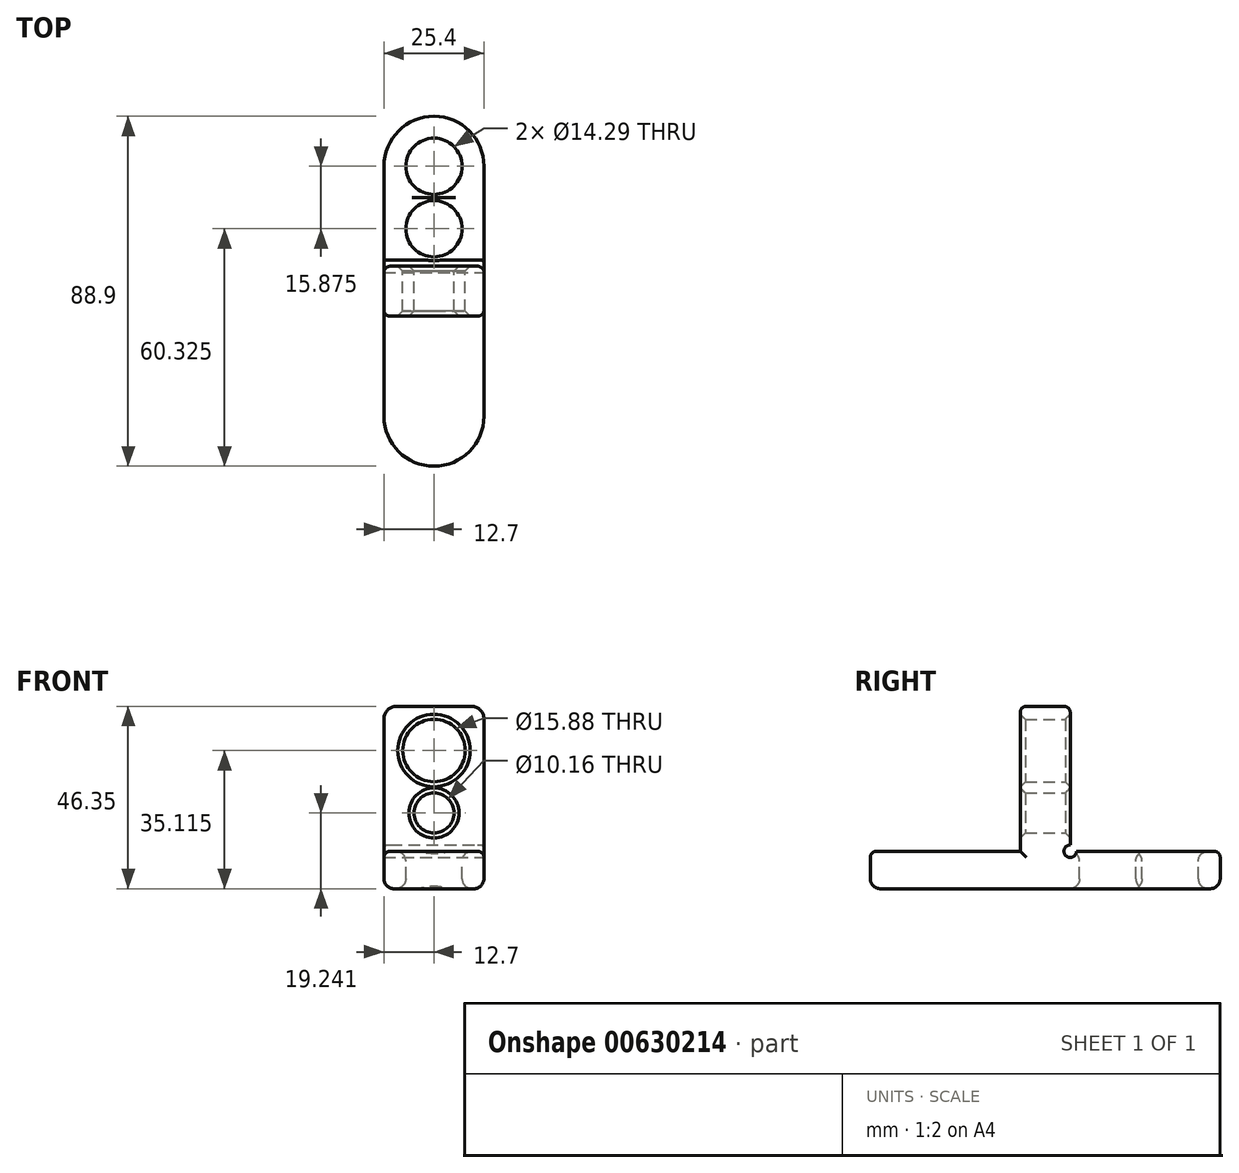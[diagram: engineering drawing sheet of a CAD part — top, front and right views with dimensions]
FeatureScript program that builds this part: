
annotation { "Feature Type Name" : "Feature", "Feature Type Description" : "" }
export const myFeature = defineFeature(function(context is Context, id is Id, definition is map)
    precondition{}
    {
        {
            var Q0;
            Q0=qCreatedBy(makeId("Top.planeOp"),FACE);
            var sketch = newSketch(context, id + "F0", { "sketchPlane" : qUnion([Q0])});
            skLineSegment(sketch, "E0.bottom", {"start": v(-12.7, 44.45) * mm, "end": v(12.7, 44.45) * mm});
            skLineSegment(sketch, "E0.top", {"start": v(-12.7, -44.45) * mm, "end": v(12.7, -44.45) * mm});
            skLineSegment(sketch, "E0.left", {"start": v(-12.7, 44.45) * mm, "end": v(-12.7, -44.45) * mm});
            skLineSegment(sketch, "E0.right", {"start": v(12.7, 44.45) * mm, "end": v(12.7, -44.45) * mm});
            skPoint(sketch, "E0.middle", {"position": v(0, 0) * mm});
            skSolve(sketch);
        }
        {
            var Q0;
            Q0=makeQuery(id+"F0.imprint","IMPRINT",FACE,{"disambiguationData":[TD([[makeQuery(id+"F0.imprint","IMPRINT",EDGE,{"derivedFrom":sQuery(id+"F0.wireOp",EDGE,"E0.bottom")}),-1.0]])]});
            extrude(context, id + "F1", {"entities" : qUnion([Q0]), "depth" : 9.52 * mm, "offsetDistance" : 25.4 * mm});
        }
        {
            var Q0;
            Q0=makeQuery(id+"F1.opExtrude","CAP_FACE",FACE,{"disambiguationData":[OSD([sQuery(id+"F0.wireOp",EDGE,"E0.bottom"),sQuery(id+"F0.wireOp",EDGE,"E0.top"),sQuery(id+"F0.wireOp",EDGE,"E0.left"),sQuery(id+"F0.wireOp",EDGE,"E0.right")])],"isStart":false});
            var sketch = newSketch(context, id + "F2", { "sketchPlane" : qUnion([Q0])});
            skLineSegment(sketch, "E1.bottom", {"start": v(-12.7, -6.35) * mm, "end": v(12.7, -6.35) * mm});
            skLineSegment(sketch, "E1.top", {"start": v(-12.7, 6.35) * mm, "end": v(12.7, 6.35) * mm});
            skLineSegment(sketch, "E1.left", {"start": v(-12.7, -6.35) * mm, "end": v(-12.7, 6.35) * mm});
            skLineSegment(sketch, "E1.right", {"start": v(12.7, -6.35) * mm, "end": v(12.7, 6.35) * mm});
            skPoint(sketch, "E1.middle", {"position": v(0, 0) * mm});
            skSolve(sketch);
        }
        {
            var Q0;
            Q0=makeQuery(id+"F2.imprint","IMPRINT",FACE,{"disambiguationData":[TD([[makeQuery(id+"F2.imprint","IMPRINT",EDGE,{"derivedFrom":sQuery(id+"F2.wireOp",EDGE,"E1.bottom")}),1.0]])]});
            extrude(context, id + "F3", {"entities" : qUnion([Q0]), "operationType" : NewBodyOperationType.ADD, "depth" : 36.83 * mm, "offsetDistance" : 25.4 * mm});
        }
        {
            var Q0;
            Q0=makeQuery(id+"F3.opExtrude","SWEPT_FACE",FACE,{"disambiguationData":[OSD([sQuery(id+"F2.wireOp",EDGE,"E1.top")])]});
            var sketch = newSketch(context, id + "F4", { "sketchPlane" : qUnion([Q0])});
            skCircle(sketch, "E2", {"center": v(0, 19.24) * mm, "radius": 5.08 * mm});
            skPoint(sketch, "E2.centerSnap0", {"position": v(0, 46.35) * mm});
            skCircle(sketch, "E3", {"center": v(0, 35.12) * mm, "radius": 7.94 * mm});
            skSolve(sketch);
        }
        {
            var Q0;
            Q0=makeQuery(id+"F4.imprint","IMPRINT",FACE,{"disambiguationData":[TD([[makeQuery(id+"F4.imprint","IMPRINT",EDGE,{"derivedFrom":sQuery(id+"F4.wireOp",EDGE,"E2")}),1.0]])]});
            var Q1;
            Q1=makeQuery(id+"F4.imprint","IMPRINT",FACE,{"disambiguationData":[TD([[makeQuery(id+"F4.imprint","IMPRINT",EDGE,{"derivedFrom":sQuery(id+"F4.wireOp",EDGE,"E3")}),1.0]])]});
            extrude(context, id + "F5", {"entities" : qUnion([Q0, Q1]), "operationType" : NewBodyOperationType.REMOVE, "endBound" : BoundingType.THROUGH_ALL, "oppositeDirection" : true, "depth" : 25.4 * mm, "offsetDistance" : 25.4 * mm});
        }
        {
            var Q0;
            Q0=makeQuery(id+"F5.boolean.opBoolean","COPY",FACE,{"derivedFrom":makeQuery(id+"F5.opExtrude","SWEPT_FACE",FACE,{"disambiguationData":[OSD([sQuery(id+"F4.wireOp",EDGE,"E2")])]})});
            var Q1;
            Q1=makeQuery(id+"F5.boolean.opBoolean","COPY",FACE,{"derivedFrom":makeQuery(id+"F5.opExtrude","SWEPT_FACE",FACE,{"disambiguationData":[OSD([sQuery(id+"F4.wireOp",EDGE,"E3")])]})});
            chamfer(context, id + "F6", {"entities" : qUnion([Q0, Q1]), "width" : 1.27 * mm, "tangentPropagation" : true});
        }
        {
            var Q0;
            Q0=makeQuery(id+"F3.opExtrude","CAP_EDGE",EDGE,{"disambiguationData":[OSD([sQuery(id+"F2.wireOp",EDGE,"E1.left")])],"isStart":false});
            var Q1;
            Q1=makeQuery(id+"F3.opExtrude","CAP_EDGE",EDGE,{"disambiguationData":[OSD([sQuery(id+"F2.wireOp",EDGE,"E1.right")])],"isStart":false});
            fillet(context, id + "F7", {"entities" : qUnion([Q0, Q1]), "radius" : 3.17 * mm, "tangentPropagation" : true, "allowEdgeOverflow" : false});
        }
        {
            var Q0;
            Q0=makeQuery(id+"F1.opExtrude","SWEPT_EDGE",EDGE,{"disambiguationData":[OSD([sQuery(id+"F0.wireOp",EDGE,"E0.bottom"),sQuery(id+"F0.wireOp",EDGE,"E0.left")])]});
            var Q1;
            Q1=makeQuery(id+"F1.opExtrude","SWEPT_EDGE",EDGE,{"disambiguationData":[OSD([sQuery(id+"F0.wireOp",EDGE,"E0.bottom"),sQuery(id+"F0.wireOp",EDGE,"E0.right")])]});
            var Q2;
            Q2=makeQuery(id+"F1.opExtrude","SWEPT_EDGE",EDGE,{"disambiguationData":[OSD([sQuery(id+"F0.wireOp",EDGE,"E0.top"),sQuery(id+"F0.wireOp",EDGE,"E0.left")])]});
            var Q3;
            Q3=makeQuery(id+"F1.opExtrude","SWEPT_EDGE",EDGE,{"disambiguationData":[OSD([sQuery(id+"F0.wireOp",EDGE,"E0.top"),sQuery(id+"F0.wireOp",EDGE,"E0.right")])]});
            fillet(context, id + "F8", {"entities" : qUnion([Q0, Q1, Q2, Q3]), "radius" : 12.7 * mm, "tangentPropagation" : true, "allowEdgeOverflow" : false});
        }
        {
            var Q0;
            {var subQ0=sQuery(id+"F0.wireOp",EDGE,"E0.left");var subQ1=sQuery(id+"F0.wireOp",EDGE,"E0.right");var subQ2=sQuery(id+"F0.wireOp",EDGE,"E0.bottom");Q0=makeQuery(id+"F3.boolean.opBoolean","SPLIT",FACE,{"disambiguationData":[TD([makeQuery(id+"F1.opExtrude","SWEPT_FACE",FACE,{"disambiguationData":[OSD([subQ2])]})])],"derivedFrom":makeQuery(id+"F1.opExtrude","CAP_FACE",FACE,{"disambiguationData":[OSD([subQ2,sQuery(id+"F0.wireOp",EDGE,"E0.top"),subQ0,subQ1])],"isStart":false})});}
            var sketch = newSketch(context, id + "F9", { "sketchPlane" : qUnion([Q0])});
            skLineSegment(sketch, "E4", {"start": v(-12.7, 0) * mm, "end": v(12.7, 0) * mm, "construction": true});
            skCircle(sketch, "E5", {"center": v(0, 31.75) * mm, "radius": 7.14 * mm});
            skCircle(sketch, "E6.MirrorC", {"center": v(0, -31.75) * mm, "radius": 7.14 * mm});
            skCircle(sketch, "E7", {"center": v(0, 15.88) * mm, "radius": 7.14 * mm});
            skCircle(sketch, "E8.MirrorC", {"center": v(0, -15.88) * mm, "radius": 7.14 * mm});
            skSolve(sketch);
        }
        {
            var Q0;
            Q0=makeQuery(id+"F9.imprint","IMPRINT",FACE,{"disambiguationData":[TD([[makeQuery(id+"F9.imprint","IMPRINT",EDGE,{"derivedFrom":sQuery(id+"F9.wireOp",EDGE,"E5")}),1.0]])]});
            var Q1;
            Q1=makeQuery(id+"F9.imprint","IMPRINT",FACE,{"disambiguationData":[TD([[makeQuery(id+"F9.imprint","IMPRINT",EDGE,{"derivedFrom":sQuery(id+"F9.wireOp",EDGE,"E6.MirrorC")}),-1.0]])]});
            var Q2;
            Q2=makeQuery(id+"F9.imprint","IMPRINT",FACE,{"disambiguationData":[TD([[makeQuery(id+"F9.imprint","IMPRINT",EDGE,{"derivedFrom":sQuery(id+"F9.wireOp",EDGE,"g7B6Eq3x-FfVw-eZ92-vdWZ-8Vn6hrICvNFo")}),1.0]])]});
            var Q3;
            Q3=makeQuery(id+"F9.imprint","IMPRINT",FACE,{"disambiguationData":[TD([[makeQuery(id+"F9.imprint","IMPRINT",EDGE,{"derivedFrom":sQuery(id+"F9.wireOp",EDGE,"E7")}),1.0]])]});
            var Q4;
            Q4=makeQuery(id+"F9.imprint","IMPRINT",FACE,{"disambiguationData":[TD([[makeQuery(id+"F9.imprint","IMPRINT",EDGE,{"derivedFrom":sQuery(id+"F9.wireOp",EDGE,"f2550661-a9b6-4266-a2c0-eb8fd2ea3ddd0.MirrorC")}),-1.0]])]});
            var Q5;
            Q5=makeQuery(id+"F9.imprint","IMPRINT",FACE,{"disambiguationData":[TD([[makeQuery(id+"F9.imprint","IMPRINT",EDGE,{"derivedFrom":sQuery(id+"F9.wireOp",EDGE,"E8.MirrorC")}),-1.0]])]});
            extrude(context, id + "F10", {"entities" : qUnion([Q0, Q1, Q2, Q3, Q4, Q5]), "operationType" : NewBodyOperationType.REMOVE, "endBound" : BoundingType.THROUGH_ALL, "oppositeDirection" : true, "depth" : 25.4 * mm, "offsetDistance" : 25.4 * mm});
        }
        {
            var Q0;
            Q0=makeQuery(id+"F3.boolean.opBoolean","MERGE",FACE,{"derivedFrom":[makeQuery(id+"F1.opExtrude","SWEPT_FACE",FACE,{"disambiguationData":[OSD([sQuery(id+"F0.wireOp",EDGE,"E0.right")])]}),makeQuery(id+"F3.opExtrude","SWEPT_FACE",FACE,{"disambiguationData":[OSD([sQuery(id+"F2.wireOp",EDGE,"E1.right")])]})]});
            var sketch = newSketch(context, id + "F11", { "sketchPlane" : qUnion([Q0])});
            skCircle(sketch, "E9", {"center": v(6.35, 9.53) * mm, "radius": 1.59 * mm});
            skLineSegment(sketch, "E10", {"start": v(0, 43.18) * mm, "end": v(0, 0) * mm, "construction": true});
            skCircle(sketch, "E11.MirrorC", {"center": v(-6.35, 9.53) * mm, "radius": 1.59 * mm});
            skSolve(sketch);
        }
        {
            var Q0;
            {var subQ0=sQuery(id+"F11.wireOp",EDGE,"E11.MirrorC");var subQ1=sQuery(id+"F2.wireOp",EDGE,"E1.right");var subQ2=sQuery(id+"F2.wireOp",EDGE,"E1.bottom");var subQ3=sQuery(id+"F0.wireOp",EDGE,"E0.right");var subQ4=makeQuery(id+"F3.opExtrude","SWEPT_EDGE",EDGE,{"disambiguationData":[OSD([subQ3,subQ2,subQ1])]});var subQ5=makeQuery(id+"F11.imprint","INTERSECT",VERTEX,{"derivedFrom":[subQ4,subQ0]});Q0=makeQuery(id+"F11.imprint","IMPRINT",FACE,{"disambiguationData":[TD([[makeQuery(id+"F11.imprint","IMPRINT",EDGE,{"disambiguationData":[TD([[subQ5,-1.0]])],"derivedFrom":subQ0}),-1.0]])]});}
            var Q1;
            {var subQ0=sQuery(id+"F11.wireOp",EDGE,"E9");var subQ1=sQuery(id+"F2.wireOp",EDGE,"E1.right");var subQ2=sQuery(id+"F2.wireOp",EDGE,"E1.top");var subQ3=sQuery(id+"F0.wireOp",EDGE,"E0.right");var subQ4=makeQuery(id+"F3.opExtrude","SWEPT_EDGE",EDGE,{"disambiguationData":[OSD([subQ3,subQ2,subQ1])]});var subQ5=makeQuery(id+"F11.imprint","INTERSECT",VERTEX,{"derivedFrom":[subQ4,subQ0]});Q1=makeQuery(id+"F11.imprint","IMPRINT",FACE,{"disambiguationData":[TD([[makeQuery(id+"F11.imprint","IMPRINT",EDGE,{"disambiguationData":[TD([[subQ5,-1.0]])],"derivedFrom":subQ0}),1.0]])]});}
            extrude(context, id + "F12", {"entities" : qUnion([Q0, Q1]), "operationType" : NewBodyOperationType.REMOVE, "endBound" : BoundingType.THROUGH_ALL, "oppositeDirection" : true, "depth" : 25.4 * mm, "offsetDistance" : 25.4 * mm});
        }
        {
            var Q0;
            Q0=makeQuery(id+"F10.boolean.opBoolean","COPY",FACE,{"derivedFrom":makeQuery(id+"F10.opExtrude","SWEPT_FACE",FACE,{"disambiguationData":[OSD([sQuery(id+"F9.wireOp",EDGE,"E5")])]})});
            var Q1;
            Q1=makeQuery(id+"F10.boolean.opBoolean","COPY",FACE,{"derivedFrom":makeQuery(id+"F10.opExtrude","SWEPT_FACE",FACE,{"disambiguationData":[OSD([sQuery(id+"F9.wireOp",EDGE,"E6.MirrorC")])]})});
            var Q2;
            Q2=makeQuery(id+"F1.opExtrude","CAP_FACE",FACE,{"disambiguationData":[OSD([sQuery(id+"F0.wireOp",EDGE,"E0.bottom"),sQuery(id+"F0.wireOp",EDGE,"E0.top"),sQuery(id+"F0.wireOp",EDGE,"E0.left"),sQuery(id+"F0.wireOp",EDGE,"E0.right")])],"isStart":true});
            var Q3;
            Q3=makeQuery(id+"F10.boolean.opBoolean","COPY",FACE,{"derivedFrom":makeQuery(id+"F10.opExtrude","SWEPT_FACE",FACE,{"disambiguationData":[OSD([sQuery(id+"F9.wireOp",EDGE,"g7B6Eq3x-FfVw-eZ92-vdWZ-8Vn6hrICvNFo")])]})});
            var Q4;
            Q4=makeQuery(id+"F10.boolean.opBoolean","COPY",FACE,{"derivedFrom":makeQuery(id+"F10.opExtrude","SWEPT_FACE",FACE,{"disambiguationData":[OSD([sQuery(id+"F9.wireOp",EDGE,"E7")])]})});
            var Q5;
            Q5=makeQuery(id+"F10.boolean.opBoolean","COPY",FACE,{"derivedFrom":makeQuery(id+"F10.opExtrude","SWEPT_FACE",FACE,{"disambiguationData":[OSD([sQuery(id+"F9.wireOp",EDGE,"E8.MirrorC")])]})});
            var Q6;
            Q6=makeQuery(id+"F10.boolean.opBoolean","COPY",FACE,{"derivedFrom":makeQuery(id+"F10.opExtrude","SWEPT_FACE",FACE,{"disambiguationData":[OSD([sQuery(id+"F9.wireOp",EDGE,"f2550661-a9b6-4266-a2c0-eb8fd2ea3ddd0.MirrorC")])]})});
            fillet(context, id + "F13", {"entities" : qUnion([Q0, Q1, Q2, Q3, Q4, Q5, Q6]), "radius" : 2.54 * mm, "tangentPropagation" : true, "allowEdgeOverflow" : false});
        }
        {
            var Q0;
            Q0=makeQuery(id+"F3.opExtrude","CAP_EDGE",EDGE,{"disambiguationData":[OSD([sQuery(id+"F2.wireOp",EDGE,"E1.bottom")])],"isStart":false});
            var Q1;
            Q1=makeQuery(id+"F3.opExtrude","CAP_EDGE",EDGE,{"disambiguationData":[OSD([sQuery(id+"F2.wireOp",EDGE,"E1.top")])],"isStart":false});
            var Q2;
            {var subQ0=sQuery(id+"F0.wireOp",EDGE,"E0.right");var subQ1=sQuery(id+"F0.wireOp",EDGE,"E0.bottom");Q2=makeQuery(id+"F3.boolean.opBoolean","SPLIT",EDGE,{"disambiguationData":[TD([makeQuery(id+"F1.opExtrude","SWEPT_FACE",FACE,{"disambiguationData":[OSD([subQ1])]})])],"derivedFrom":makeQuery(id+"F1.opExtrude","CAP_EDGE",EDGE,{"disambiguationData":[OSD([subQ0])],"isStart":false})});}
            var Q3;
            {var subQ0=sQuery(id+"F0.wireOp",EDGE,"E0.right");var subQ1=sQuery(id+"F0.wireOp",EDGE,"E0.top");Q3=makeQuery(id+"F3.boolean.opBoolean","SPLIT",EDGE,{"disambiguationData":[TD([makeQuery(id+"F1.opExtrude","SWEPT_FACE",FACE,{"disambiguationData":[OSD([subQ1])]})])],"derivedFrom":makeQuery(id+"F1.opExtrude","CAP_EDGE",EDGE,{"disambiguationData":[OSD([subQ0])],"isStart":false})});}
            fillet(context, id + "F14", {"entities" : qUnion([Q0, Q1, Q2, Q3]), "radius" : 1.59 * mm, "tangentPropagation" : true, "allowEdgeOverflow" : false});
        }
    });
